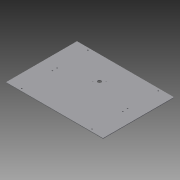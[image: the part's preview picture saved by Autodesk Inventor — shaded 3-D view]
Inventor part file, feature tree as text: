
AUTODESK INVENTOR PART (.ipt)
format: ipt  version: 2015 SP1 (Build 190203100, 203)  size: 121,856 bytes
history: native  units: in
note: dims shown in document units (in); Inventor stores cm internally (conversion verified against a paired STEP export)
features: sketch x4, projected_geometry x3, extrude x2, hole x2
ambient origin geometry x8: Origin, YZ Plane, XZ Plane, XY Plane, X Axis, Y Axis, Z Axis, Center Point
bodies: Solid1 (feature_tree)
feature tree (11):
  extrude  "Extrusion1"  Depth=15.0in
  hole  "Hole1"  [1 undecoded]
  hole  "Hole2"  [1 undecoded]
  extrude  "Extrusion2"  Depth=0.125in
  sketch  "Sketch1"  dims[d0=20.5in d1=15.0in]
  sketch  "Sketch2"  dims[d2=0.125in d3=0.0in d4=2.3125in]
  projected_geometry  "Projected Loop1"
  sketch  "Sketch3"  dims[d5=2.3125in d6=2.3125in]
  projected_geometry  "Projected Loop2"
  sketch  "Sketch4"  dims[d7=2.3125in d8=0.5in d9=0.5in d10=0.5in d11=0.5in d12=0.25in d13=0.75in d14=0.375in d15=0.25in d16=0.5635in d17=1.0in d18=0.8108in d19=7.0in d20=7.0in d21=7.0in d22=7.0in d23=2.3125in d24=2.3125in d25=2.3125in d26=2.3125in d27=0.25in d28=0.75in d29=0.375in d30=0.25in d31=0.5635in d32=1.0in d33=0.8108in d34=0.75in d35=5.0in d36=10.25in d37=1.0in d38=135.0deg d39=1.0in d40=45.0deg d41=0.1562in d42=0.1562in d43=0.125in d44=0.0in]
  projected_geometry  "Projected Loop3"
note: 2 required parameter values undecoded (feature->parameter linkage not recoverable at this tier; creation-order binding heuristic only, values carry confidence <= 0.55)
